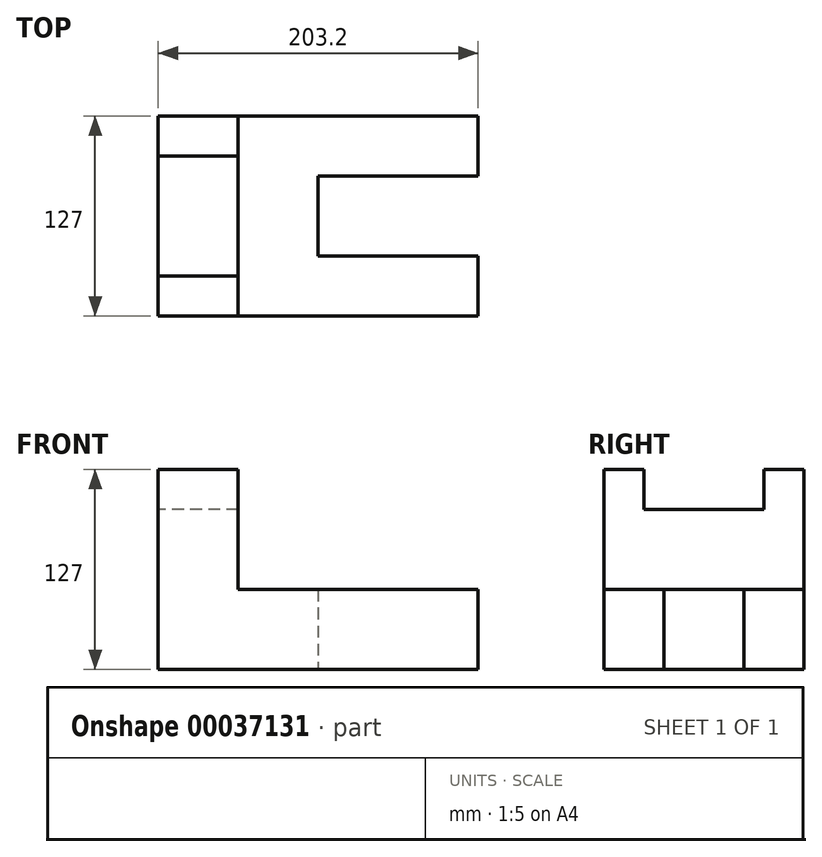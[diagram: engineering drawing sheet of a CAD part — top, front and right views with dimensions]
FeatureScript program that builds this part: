
annotation { "Feature Type Name" : "Feature", "Feature Type Description" : "" }
export const myFeature = defineFeature(function(context is Context, id is Id, definition is map)
    precondition{}
    {
        {
            var Q0;
            Q0=qCreatedBy(makeId("Top.planeOp"),FACE);
            var sketch = newSketch(context, id + "F0", { "sketchPlane" : qUnion([Q0])});
            skLineSegment(sketch, "E0", {"start": v(-119.87, 79.25) * mm, "end": v(83.33, 79.25) * mm});
            skLineSegment(sketch, "E1", {"start": v(83.33, 79.25) * mm, "end": v(83.33, 41.15) * mm});
            skLineSegment(sketch, "E2", {"start": v(83.33, 41.15) * mm, "end": v(-18.27, 41.15) * mm});
            skLineSegment(sketch, "E3", {"start": v(-18.27, 41.15) * mm, "end": v(-18.27, -9.65) * mm});
            skLineSegment(sketch, "E4", {"start": v(-18.27, -9.65) * mm, "end": v(83.33, -9.65) * mm});
            skLineSegment(sketch, "E5", {"start": v(83.33, -9.65) * mm, "end": v(83.33, -47.75) * mm});
            skLineSegment(sketch, "E6", {"start": v(83.33, -47.75) * mm, "end": v(-119.87, -47.75) * mm});
            skLineSegment(sketch, "E7", {"start": v(-119.87, -47.75) * mm, "end": v(-119.87, 79.25) * mm});
            skLineSegment(sketch, "E8", {"start": v(-119.87, 79.25) * mm, "end": v(-119.87, -47.75) * mm});
            skSolve(sketch);
        }
        {
            var Q0;
            Q0=makeQuery(id+"F0.imprint","IMPRINT",FACE,{"disambiguationData":[TD([[makeQuery(id+"F0.imprint","IMPRINT",EDGE,{"derivedFrom":sQuery(id+"F0.wireOp",EDGE,"E0")}),-1.0]])]});
            extrude(context, id + "F1", {"entities" : qUnion([Q0]), "depth" : 50.8 * mm});
        }
        {
            var Q0;
            Q0=makeQuery(id+"F1.opExtrude","CAP_FACE",FACE,{"disambiguationData":[OSD([sQuery(id+"F0.wireOp",EDGE,"E0"),sQuery(id+"F0.wireOp",EDGE,"E1"),sQuery(id+"F0.wireOp",EDGE,"E2"),sQuery(id+"F0.wireOp",EDGE,"E3"),sQuery(id+"F0.wireOp",EDGE,"E4"),sQuery(id+"F0.wireOp",EDGE,"E5"),sQuery(id+"F0.wireOp",EDGE,"E6"),sQuery(id+"F0.wireOp",EDGE,"E8")])],"isStart":false});
            var sketch = newSketch(context, id + "F2", { "sketchPlane" : qUnion([Q0])});
            skLineSegment(sketch, "E9", {"start": v(-119.87, 79.25) * mm, "end": v(-69.07, 79.25) * mm});
            skLineSegment(sketch, "E10", {"start": v(-69.07, 79.25) * mm, "end": v(-69.07, -47.75) * mm});
            skLineSegment(sketch, "E11", {"start": v(-69.07, -47.75) * mm, "end": v(-119.87, -47.75) * mm});
            skLineSegment(sketch, "E12", {"start": v(-119.87, -47.75) * mm, "end": v(-119.87, 79.25) * mm});
            skSolve(sketch);
        }
        {
            var Q0;
            Q0=makeQuery(id+"F2.imprint","IMPRINT",FACE,{"disambiguationData":[TD([[makeQuery(id+"F2.imprint","IMPRINT",EDGE,{"derivedFrom":sQuery(id+"F2.wireOp",EDGE,"E9")}),-1.0]])]});
            extrude(context, id + "F3", {"entities" : qUnion([Q0]), "operationType" : NewBodyOperationType.ADD, "depth" : 50.8 * mm});
        }
        {
            var Q0;
            Q0=makeQuery(id+"F3.opExtrude","CAP_FACE",FACE,{"disambiguationData":[OSD([sQuery(id+"F2.wireOp",EDGE,"E9"),sQuery(id+"F2.wireOp",EDGE,"E10"),sQuery(id+"F2.wireOp",EDGE,"E11"),sQuery(id+"F2.wireOp",EDGE,"E12")])],"isStart":false});
            var sketch = newSketch(context, id + "F4", { "sketchPlane" : qUnion([Q0])});
            skLineSegment(sketch, "E13", {"start": v(-119.87, 79.25) * mm, "end": v(-69.07, 79.25) * mm});
            skLineSegment(sketch, "E14", {"start": v(-69.07, 79.25) * mm, "end": v(-69.07, 53.85) * mm});
            skLineSegment(sketch, "E15", {"start": v(-69.07, 53.85) * mm, "end": v(-119.87, 53.85) * mm});
            skLineSegment(sketch, "E16", {"start": v(-119.87, 53.85) * mm, "end": v(-119.87, 79.25) * mm});
            skLineSegment(sketch, "E17", {"start": v(-119.87, -47.75) * mm, "end": v(-69.07, -47.75) * mm});
            skLineSegment(sketch, "E18", {"start": v(-69.07, -47.75) * mm, "end": v(-69.07, -22.35) * mm});
            skLineSegment(sketch, "E19", {"start": v(-69.07, -22.35) * mm, "end": v(-119.87, -22.35) * mm});
            skSolve(sketch);
        }
        {
            var Q0;
            {var subQ2=sQuery(id+"F4.wireOp",EDGE,"E17");Q0=makeQuery(id+"F4.imprint","IMPRINT",FACE,{"disambiguationData":[TD([[makeQuery(id+"F4.imprint","IMPRINT",EDGE,{"derivedFrom":subQ2}),-1.0]])]});}
            extrude(context, id + "F5", {"entities" : qUnion([Q0]), "operationType" : NewBodyOperationType.ADD, "depth" : 25.4 * mm});
        }
        {
            var Q0;
            Q0=makeQuery(id+"F3.opExtrude","CAP_FACE",FACE,{"disambiguationData":[OSD([sQuery(id+"F2.wireOp",EDGE,"E9"),sQuery(id+"F2.wireOp",EDGE,"E10"),sQuery(id+"F2.wireOp",EDGE,"E11"),sQuery(id+"F2.wireOp",EDGE,"E12")])],"isStart":false});
            var sketch = newSketch(context, id + "F6", { "sketchPlane" : qUnion([Q0])});
            skLineSegment(sketch, "E20", {"start": v(-119.87, 79.25) * mm, "end": v(-69.07, 79.25) * mm});
            skLineSegment(sketch, "E21", {"start": v(-69.07, 79.25) * mm, "end": v(-69.07, 53.85) * mm});
            skLineSegment(sketch, "E22", {"start": v(-69.07, 53.85) * mm, "end": v(-119.87, 53.85) * mm});
            skLineSegment(sketch, "E23", {"start": v(-119.87, 53.85) * mm, "end": v(-119.87, 79.25) * mm});
            skSolve(sketch);
        }
        {
            var Q0;
            Q0=makeQuery(id+"F6.imprint","IMPRINT",FACE,{"disambiguationData":[TD([[makeQuery(id+"F6.imprint","IMPRINT",EDGE,{"derivedFrom":sQuery(id+"F6.wireOp",EDGE,"E20")}),-1.0]])]});
            extrude(context, id + "F7", {"entities" : qUnion([Q0]), "operationType" : NewBodyOperationType.ADD, "depth" : 25.4 * mm});
        }
    });
